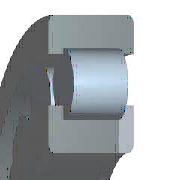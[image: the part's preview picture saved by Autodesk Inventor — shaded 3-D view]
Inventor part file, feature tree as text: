
AUTODESK INVENTOR PART (.ipt)
format: ipt  version: 2020 (Build 240168000, 168)  size: 278,016 bytes
history: native  units: mm (DEFAULTED — no unit token found)
features: sketch x1, pattern_circular x1, fillet x1
ambient origin geometry x8: Origin, YZ Plane, XZ Plane, XY Plane, X Axis, Y Axis, Z Axis, Center Point
bodies: Solid1 (feature_tree), BODY (feature_tree)
feature tree (3):
  sketch  "草图"  dims[d64=90.0deg d0=80.0mm d1=360.0deg d4=0.0mm d5=0.0mm d6=0.0mm d7=65.0mm d8=82.5mm d9=89.9mm d10=115.1mm d11=140.0mm d12=124.5mm d13=12.0mm d14=48.0mm d15=0.0mm d16=0.0mm d89=90.0deg d90=2.1mm d91=2.1mm]
  pattern_circular  "IDS_ARRAYROLLER[SIMPL:T]"  Count=8 Angle=360.0deg
  fillet  "Fillet1"  [1 undecoded]
note: 1 required parameter value undecoded (feature->parameter linkage not recoverable at this tier; creation-order binding heuristic only, values carry confidence <= 0.55)
